AUTODESK INVENTOR PART (.ipt)
format: ipt  version: 2025 (Build 290162010, 162A)  size: 183,296 bytes
history: native  units: mm
features: extrude x3, sketch x3
ambient origin geometry x8: Origin, YZ Plane, XZ Plane, XY Plane, X Axis, Y Axis, Z Axis, Center Point
bodies: Solid1 (feature_tree)
feature tree (6):
  extrude  "Extrusion1"  Depth=102.0mm
  extrude  "Extrusion2"  Depth=80.0mm
  extrude  "Extrusion3"  Depth=180.0mm TaperAngle=0.0deg
  sketch  "Sketch1"  dims[d7=285.0mm d8=102.0mm]
  sketch  "Sketch2"  dims[d9=82.0mm d13=80.0mm]
  sketch  "Sketch3"  dims[d14=80.0mm d15=180.0mm d16=0.0mm d17=190.0mm d18=170.0mm d19=10.0mm d20=0.0mm d21=138.0mm d22=102.0mm d23=0.0mm d24=0.5mm d25=0.872665mm]
